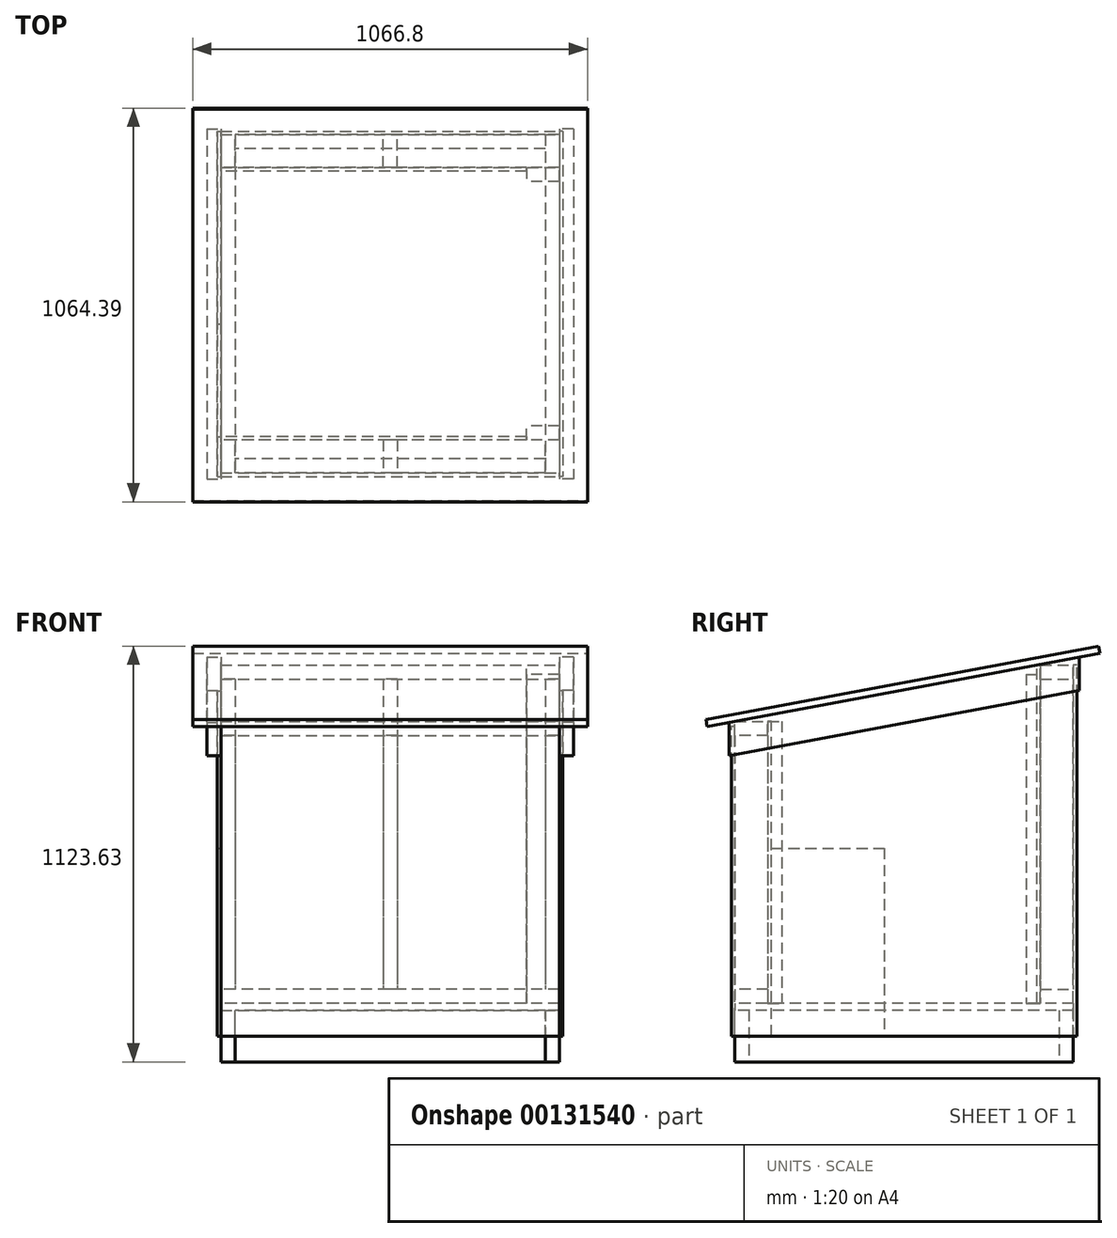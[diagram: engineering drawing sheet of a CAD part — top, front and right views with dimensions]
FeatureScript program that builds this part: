
annotation { "Feature Type Name" : "Feature", "Feature Type Description" : "" }
export const myFeature = defineFeature(function(context is Context, id is Id, definition is map)
    precondition{}
    {
        {
            var Q0;
            Q0=qCreatedBy(makeId("Front.planeOp"),FACE);
            var sketch = newSketch(context, id + "F0", { "sketchPlane" : qUnion([Q0])});
            skLineSegment(sketch, "E0.bottom", {"start": v(0, 0) * mm, "end": v(38.1, 0) * mm});
            skLineSegment(sketch, "E0.top", {"start": v(0, 139.7) * mm, "end": v(38.1, 139.7) * mm});
            skLineSegment(sketch, "E0.left", {"start": v(0, 0) * mm, "end": v(0, 139.7) * mm});
            skLineSegment(sketch, "E0.right", {"start": v(38.1, 0) * mm, "end": v(38.1, 139.7) * mm});
            skSolve(sketch);
        }
        {
            var Q0;
            Q0=qSketchRegion(id+"F0",true);
            extrude(context, id + "F1", {"entities" : qUnion([Q0]), "oppositeDirection" : true, "depth" : 914.4 * mm});
        }
        {
            var Q0;
            Q0=qCreatedBy(makeId("Front.planeOp"),FACE);
            var sketch = newSketch(context, id + "F2", { "sketchPlane" : qUnion([Q0])});
            skLineSegment(sketch, "E1.bottom", {"start": v(876.3, 0) * mm, "end": v(914.4, 0) * mm});
            skLineSegment(sketch, "E1.top", {"start": v(876.3, 139.7) * mm, "end": v(914.4, 139.7) * mm});
            skLineSegment(sketch, "E1.left", {"start": v(876.3, 0) * mm, "end": v(876.3, 139.7) * mm});
            skLineSegment(sketch, "E1.right", {"start": v(914.4, 0) * mm, "end": v(914.4, 139.7) * mm});
            skSolve(sketch);
        }
        {
            var Q0;
            Q0=makeQuery(id+"F2.imprint","IMPRINT",FACE,{"disambiguationData":[TD([[makeQuery(id+"F2.imprint","IMPRINT",EDGE,{"derivedFrom":sQuery(id+"F2.wireOp",EDGE,"E1.bottom")}),1.0]])]});
            var Q1;
            Q1=makeQuery(id+"F1.opExtrude","CAP_FACE",FACE,{"disambiguationData":[OSD([sQuery(id+"F0.wireOp",EDGE,"E0.bottom"),sQuery(id+"F0.wireOp",EDGE,"E0.top"),sQuery(id+"F0.wireOp",EDGE,"E0.left"),sQuery(id+"F0.wireOp",EDGE,"E0.right")])],"isStart":false});
            extrude(context, id + "F3", {"entities" : qUnion([Q0]), "endBound" : BoundingType.UP_TO_SURFACE, "oppositeDirection" : true, "endBoundEntityFace" : qUnion([Q1]), "depth" : 914.4 * mm});
        }
        {
            var Q0;
            Q0=makeQuery(id+"F1.opExtrude","SWEPT_FACE",FACE,{"disambiguationData":[OSD([sQuery(id+"F0.wireOp",EDGE,"E0.right")])]});
            var sketch = newSketch(context, id + "F4", { "sketchPlane" : qUnion([Q0])});
            skLineSegment(sketch, "E2.bottom", {"start": v(914.4, 139.7) * mm, "end": v(876.3, 139.7) * mm});
            skLineSegment(sketch, "E2.top", {"start": v(914.4, 0) * mm, "end": v(876.3, 0) * mm});
            skLineSegment(sketch, "E2.left", {"start": v(914.4, 139.7) * mm, "end": v(914.4, 0) * mm});
            skLineSegment(sketch, "E2.right", {"start": v(876.3, 139.7) * mm, "end": v(876.3, 0) * mm});
            skSolve(sketch);
        }
        {
            var Q0;
            Q0=qSketchRegion(id+"F4",true);
            var Q1;
            Q1=makeQuery(id+"F3.opExtrude","SWEPT_BODY",BODY,{"disambiguationData":[OSD([sQuery(id+"F2.wireOp",EDGE,"E1.bottom"),sQuery(id+"F2.wireOp",EDGE,"E1.top"),sQuery(id+"F2.wireOp",EDGE,"E1.left"),sQuery(id+"F2.wireOp",EDGE,"E1.right")])]});
            extrude(context, id + "F5", {"entities" : qUnion([Q0]), "endBound" : BoundingType.UP_TO_BODY, "endBoundEntityBody" : qUnion([Q1]), "depth" : 25.4 * mm});
        }
        {
            var Q0;
            Q0=makeQuery(id+"F1.opExtrude","SWEPT_FACE",FACE,{"disambiguationData":[OSD([sQuery(id+"F0.wireOp",EDGE,"E0.right")])]});
            var sketch = newSketch(context, id + "F6", { "sketchPlane" : qUnion([Q0])});
            skLineSegment(sketch, "E3.bottom", {"start": v(0, 139.7) * mm, "end": v(38.1, 139.7) * mm});
            skLineSegment(sketch, "E3.top", {"start": v(0, 0) * mm, "end": v(38.1, 0) * mm});
            skLineSegment(sketch, "E3.left", {"start": v(0, 139.7) * mm, "end": v(0, 0) * mm});
            skLineSegment(sketch, "E3.right", {"start": v(38.1, 139.7) * mm, "end": v(38.1, 0) * mm});
            skSolve(sketch);
        }
        {
            var Q0;
            Q0=qSketchRegion(id+"F6",true);
            var Q1;
            Q1=makeQuery(id+"F3.opExtrude","SWEPT_BODY",BODY,{"disambiguationData":[OSD([sQuery(id+"F2.wireOp",EDGE,"E1.bottom"),sQuery(id+"F2.wireOp",EDGE,"E1.top"),sQuery(id+"F2.wireOp",EDGE,"E1.left"),sQuery(id+"F2.wireOp",EDGE,"E1.right")])]});
            extrude(context, id + "F7", {"entities" : qUnion([Q0]), "endBound" : BoundingType.UP_TO_BODY, "endBoundEntityBody" : qUnion([Q1]), "depth" : 25.4 * mm});
        }
        {
            var Q0;
            Q0=makeQuery(id+"F1.opExtrude","SWEPT_FACE",FACE,{"disambiguationData":[OSD([sQuery(id+"F0.wireOp",EDGE,"E0.top")])]});
            var sketch = newSketch(context, id + "F8", { "sketchPlane" : qUnion([Q0])});
            skLineSegment(sketch, "E4.bottom", {"start": v(0, 0) * mm, "end": v(914.4, 0) * mm});
            skLineSegment(sketch, "E4.top", {"start": v(0, 914.4) * mm, "end": v(914.4, 914.4) * mm});
            skLineSegment(sketch, "E4.left", {"start": v(0, 0) * mm, "end": v(0, 914.4) * mm});
            skLineSegment(sketch, "E4.right", {"start": v(914.4, 0) * mm, "end": v(914.4, 914.4) * mm});
            skSolve(sketch);
        }
        {
            var Q0;
            Q0=qSketchRegion(id+"F8",true);
            extrude(context, id + "F9", {"entities" : qUnion([Q0]), "depth" : 19.05 * mm});
        }
        {
            var Q0;
            Q0=makeQuery(id+"F1.opExtrude","SWEPT_FACE",FACE,{"disambiguationData":[OSD([sQuery(id+"F0.wireOp",EDGE,"E0.left")])]});
            var sketch = newSketch(context, id + "F10", { "sketchPlane" : qUnion([Q0])});
            skLineSegment(sketch, "E5.bottom", {"start": v(0, 158.75) * mm, "end": v(-88.9, 158.75) * mm});
            skLineSegment(sketch, "E5.top", {"start": v(0, 196.85) * mm, "end": v(-88.9, 196.85) * mm});
            skLineSegment(sketch, "E5.left", {"start": v(0, 158.75) * mm, "end": v(0, 196.85) * mm});
            skLineSegment(sketch, "E5.right", {"start": v(-88.9, 158.75) * mm, "end": v(-88.9, 196.85) * mm});
            skSolve(sketch);
        }
        {
            var Q0;
            Q0=qSketchRegion(id+"F10",true);
            var Q1;
            Q1=makeQuery(id+"F9.opExtrude","SWEPT_FACE",FACE,{"disambiguationData":[OSD([sQuery(id+"F8.wireOp",EDGE,"E4.right")])]});
            extrude(context, id + "F11", {"entities" : qUnion([Q0]), "endBound" : BoundingType.UP_TO_SURFACE, "oppositeDirection" : true, "endBoundEntityFace" : qUnion([Q1]), "depth" : 25.4 * mm});
        }
        {
            var Q0;
            Q0=makeQuery(id+"F1.opExtrude","SWEPT_FACE",FACE,{"disambiguationData":[OSD([sQuery(id+"F0.wireOp",EDGE,"E0.left")])]});
            var sketch = newSketch(context, id + "F12", { "sketchPlane" : qUnion([Q0])});
            skLineSegment(sketch, "E6.bottom", {"start": v(-914.4, 158.75) * mm, "end": v(-825.5, 158.75) * mm});
            skLineSegment(sketch, "E6.top", {"start": v(-914.4, 196.85) * mm, "end": v(-825.5, 196.85) * mm});
            skLineSegment(sketch, "E6.left", {"start": v(-914.4, 158.75) * mm, "end": v(-914.4, 196.85) * mm});
            skLineSegment(sketch, "E6.right", {"start": v(-825.5, 158.75) * mm, "end": v(-825.5, 196.85) * mm});
            skSolve(sketch);
        }
        {
            var Q0;
            Q0=qSketchRegion(id+"F12",true);
            var Q1;
            Q1=makeQuery(id+"F3.opExtrude","SWEPT_FACE",FACE,{"disambiguationData":[OSD([sQuery(id+"F2.wireOp",EDGE,"E1.right")])]});
            extrude(context, id + "F13", {"entities" : qUnion([Q0]), "endBound" : BoundingType.UP_TO_SURFACE, "oppositeDirection" : true, "endBoundEntityFace" : qUnion([Q1]), "depth" : 25.4 * mm});
        }
        {
            var Q0;
            Q0=makeQuery(id+"F13.opExtrude","SWEPT_FACE",FACE,{"disambiguationData":[OSD([sQuery(id+"F12.wireOp",EDGE,"E6.top")])]});
            var sketch = newSketch(context, id + "F14", { "sketchPlane" : qUnion([Q0])});
            skLineSegment(sketch, "E7.bottom", {"start": v(914.4, 914.4) * mm, "end": v(876.3, 914.4) * mm});
            skLineSegment(sketch, "E7.top", {"start": v(914.4, 825.5) * mm, "end": v(876.3, 825.5) * mm});
            skLineSegment(sketch, "E7.left", {"start": v(914.4, 914.4) * mm, "end": v(914.4, 825.5) * mm});
            skLineSegment(sketch, "E7.right", {"start": v(876.3, 914.4) * mm, "end": v(876.3, 825.5) * mm});
            skSolve(sketch);
        }
        {
            var Q0;
            Q0=qSketchRegion(id+"F14",true);
            extrude(context, id + "F15", {"entities" : qUnion([Q0]), "depth" : 838.2 * mm});
        }
        {
            var Q0;
            Q0=makeQuery(id+"F13.opExtrude","SWEPT_FACE",FACE,{"disambiguationData":[OSD([sQuery(id+"F12.wireOp",EDGE,"E6.top")])]});
            var sketch = newSketch(context, id + "F16", { "sketchPlane" : qUnion([Q0])});
            skLineSegment(sketch, "E8.bottom", {"start": v(0, 825.5) * mm, "end": v(38.1, 825.5) * mm});
            skLineSegment(sketch, "E8.top", {"start": v(0, 914.4) * mm, "end": v(38.1, 914.4) * mm});
            skLineSegment(sketch, "E8.left", {"start": v(0, 825.5) * mm, "end": v(0, 914.4) * mm});
            skLineSegment(sketch, "E8.right", {"start": v(38.1, 825.5) * mm, "end": v(38.1, 914.4) * mm});
            skSolve(sketch);
        }
        {
            var Q0;
            Q0=qSketchRegion(id+"F16",true);
            var Q1;
            Q1=makeQuery(id+"F15.opExtrude","CAP_FACE",FACE,{"disambiguationData":[OSD([sQuery(id+"F14.wireOp",EDGE,"E7.bottom"),sQuery(id+"F14.wireOp",EDGE,"E7.top"),sQuery(id+"F14.wireOp",EDGE,"E7.left"),sQuery(id+"F14.wireOp",EDGE,"E7.right")])],"isStart":false});
            extrude(context, id + "F17", {"entities" : qUnion([Q0]), "endBound" : BoundingType.UP_TO_SURFACE, "endBoundEntityFace" : qUnion([Q1]), "depth" : 25.4 * mm});
        }
        {
            var Q0;
            Q0=makeQuery(id+"F13.opExtrude","SWEPT_FACE",FACE,{"disambiguationData":[OSD([sQuery(id+"F12.wireOp",EDGE,"E6.top")])]});
            var sketch = newSketch(context, id + "F18", { "sketchPlane" : qUnion([Q0])});
            skLineSegment(sketch, "E9.bottom", {"start": v(438.15, 825.5) * mm, "end": v(476.25, 825.5) * mm});
            skLineSegment(sketch, "E9.top", {"start": v(438.15, 914.4) * mm, "end": v(476.25, 914.4) * mm});
            skLineSegment(sketch, "E9.left", {"start": v(438.15, 825.5) * mm, "end": v(438.15, 914.4) * mm});
            skLineSegment(sketch, "E9.right", {"start": v(476.25, 825.5) * mm, "end": v(476.25, 914.4) * mm});
            skSolve(sketch);
        }
        {
            var Q0;
            Q0=qSketchRegion(id+"F18",true);
            var Q1;
            Q1=makeQuery(id+"F15.opExtrude","CAP_FACE",FACE,{"disambiguationData":[OSD([sQuery(id+"F14.wireOp",EDGE,"E7.bottom"),sQuery(id+"F14.wireOp",EDGE,"E7.top"),sQuery(id+"F14.wireOp",EDGE,"E7.left"),sQuery(id+"F14.wireOp",EDGE,"E7.right")])],"isStart":false});
            extrude(context, id + "F19", {"entities" : qUnion([Q0]), "endBound" : BoundingType.UP_TO_SURFACE, "endBoundEntityFace" : qUnion([Q1]), "depth" : 25.4 * mm});
        }
        {
            var Q0;
            Q0=makeQuery(id+"F15.opExtrude","SWEPT_FACE",FACE,{"disambiguationData":[OSD([sQuery(id+"F14.wireOp",EDGE,"E7.left")])]});
            var sketch = newSketch(context, id + "F20", { "sketchPlane" : qUnion([Q0])});
            skLineSegment(sketch, "E10.bottom", {"start": v(914.4, 1035.05) * mm, "end": v(825.5, 1035.05) * mm});
            skLineSegment(sketch, "E10.top", {"start": v(914.4, 1073.15) * mm, "end": v(825.5, 1073.15) * mm});
            skLineSegment(sketch, "E10.left", {"start": v(914.4, 1035.05) * mm, "end": v(914.4, 1073.15) * mm});
            skLineSegment(sketch, "E10.right", {"start": v(825.5, 1035.05) * mm, "end": v(825.5, 1073.15) * mm});
            skSolve(sketch);
        }
        {
            var Q0;
            Q0=qSketchRegion(id+"F20",true);
            var Q1;
            Q1=makeQuery(id+"F17.opExtrude","SWEPT_FACE",FACE,{"disambiguationData":[OSD([sQuery(id+"F16.wireOp",EDGE,"E8.left")])]});
            extrude(context, id + "F21", {"entities" : qUnion([Q0]), "endBound" : BoundingType.UP_TO_SURFACE, "oppositeDirection" : true, "endBoundEntityFace" : qUnion([Q1]), "depth" : 25.4 * mm});
        }
        {
            var Q0;
            Q0=makeQuery(id+"F11.opExtrude","SWEPT_FACE",FACE,{"disambiguationData":[OSD([sQuery(id+"F10.wireOp",EDGE,"E5.top")])]});
            var sketch = newSketch(context, id + "F22", { "sketchPlane" : qUnion([Q0])});
            skLineSegment(sketch, "E11.bottom", {"start": v(914.4, 0) * mm, "end": v(876.3, 0) * mm});
            skLineSegment(sketch, "E11.top", {"start": v(914.4, 88.9) * mm, "end": v(876.3, 88.9) * mm});
            skLineSegment(sketch, "E11.left", {"start": v(914.4, 0) * mm, "end": v(914.4, 88.9) * mm});
            skLineSegment(sketch, "E11.right", {"start": v(876.3, 0) * mm, "end": v(876.3, 88.9) * mm});
            skSolve(sketch);
        }
        {
            var Q0;
            Q0=qSketchRegion(id+"F22",true);
            extrude(context, id + "F23", {"entities" : qUnion([Q0]), "depth" : 685.8 * mm});
        }
        {
            var Q0;
            Q0=makeQuery(id+"F11.opExtrude","SWEPT_FACE",FACE,{"disambiguationData":[OSD([sQuery(id+"F10.wireOp",EDGE,"E5.top")])]});
            var sketch = newSketch(context, id + "F24", { "sketchPlane" : qUnion([Q0])});
            skLineSegment(sketch, "E12.bottom", {"start": v(0, 0) * mm, "end": v(38.1, 0) * mm});
            skLineSegment(sketch, "E12.top", {"start": v(0, 88.9) * mm, "end": v(38.1, 88.9) * mm});
            skLineSegment(sketch, "E12.left", {"start": v(0, 0) * mm, "end": v(0, 88.9) * mm});
            skLineSegment(sketch, "E12.right", {"start": v(38.1, 0) * mm, "end": v(38.1, 88.9) * mm});
            skSolve(sketch);
        }
        {
            var Q0;
            Q0=qSketchRegion(id+"F24",true);
            var Q1;
            Q1=makeQuery(id+"F23.opExtrude","CAP_FACE",FACE,{"disambiguationData":[OSD([sQuery(id+"F22.wireOp",EDGE,"E11.bottom"),sQuery(id+"F22.wireOp",EDGE,"E11.top"),sQuery(id+"F22.wireOp",EDGE,"E11.left"),sQuery(id+"F22.wireOp",EDGE,"E11.right")])],"isStart":false});
            extrude(context, id + "F25", {"entities" : qUnion([Q0]), "endBound" : BoundingType.UP_TO_SURFACE, "endBoundEntityFace" : qUnion([Q1]), "depth" : 25.4 * mm});
        }
        {
            var Q0;
            Q0=makeQuery(id+"F11.opExtrude","SWEPT_FACE",FACE,{"disambiguationData":[OSD([sQuery(id+"F10.wireOp",EDGE,"E5.top")])]});
            var sketch = newSketch(context, id + "F26", { "sketchPlane" : qUnion([Q0])});
            skLineSegment(sketch, "E13.bottom", {"start": v(438.15, 88.9) * mm, "end": v(476.25, 88.9) * mm});
            skLineSegment(sketch, "E13.top", {"start": v(438.15, 0) * mm, "end": v(476.25, 0) * mm});
            skLineSegment(sketch, "E13.left", {"start": v(438.15, 88.9) * mm, "end": v(438.15, 0) * mm});
            skLineSegment(sketch, "E13.right", {"start": v(476.25, 88.9) * mm, "end": v(476.25, 0) * mm});
            skSolve(sketch);
        }
        {
            var Q0;
            Q0=qSketchRegion(id+"F26",true);
            var Q1;
            Q1=makeQuery(id+"F23.opExtrude","CAP_FACE",FACE,{"disambiguationData":[OSD([sQuery(id+"F22.wireOp",EDGE,"E11.bottom"),sQuery(id+"F22.wireOp",EDGE,"E11.top"),sQuery(id+"F22.wireOp",EDGE,"E11.left"),sQuery(id+"F22.wireOp",EDGE,"E11.right")])],"isStart":false});
            extrude(context, id + "F27", {"entities" : qUnion([Q0]), "endBound" : BoundingType.UP_TO_SURFACE, "endBoundEntityFace" : qUnion([Q1]), "depth" : 25.4 * mm});
        }
        {
            var Q0;
            Q0=makeQuery(id+"F23.opExtrude","SWEPT_FACE",FACE,{"disambiguationData":[OSD([sQuery(id+"F22.wireOp",EDGE,"E11.left")])]});
            var sketch = newSketch(context, id + "F28", { "sketchPlane" : qUnion([Q0])});
            skLineSegment(sketch, "E14.bottom", {"start": v(0, 882.65) * mm, "end": v(88.9, 882.65) * mm});
            skLineSegment(sketch, "E14.top", {"start": v(0, 920.75) * mm, "end": v(88.9, 920.75) * mm});
            skLineSegment(sketch, "E14.left", {"start": v(0, 882.65) * mm, "end": v(0, 920.75) * mm});
            skLineSegment(sketch, "E14.right", {"start": v(88.9, 882.65) * mm, "end": v(88.9, 920.75) * mm});
            skSolve(sketch);
        }
        {
            var Q0;
            Q0=qSketchRegion(id+"F28",true);
            var Q1;
            Q1=makeQuery(id+"F25.opExtrude","SWEPT_FACE",FACE,{"disambiguationData":[OSD([sQuery(id+"F24.wireOp",EDGE,"E12.left")])]});
            extrude(context, id + "F29", {"entities" : qUnion([Q0]), "endBound" : BoundingType.UP_TO_SURFACE, "oppositeDirection" : true, "endBoundEntityFace" : qUnion([Q1]), "depth" : 25.4 * mm});
        }
        {
            var Q0;
            Q0=makeQuery(id+"F13.opExtrude","SWEPT_FACE",FACE,{"disambiguationData":[OSD([sQuery(id+"F12.wireOp",EDGE,"E6.right")])]});
            var sketch = newSketch(context, id + "F30", { "sketchPlane" : qUnion([Q0])});
            skLineSegment(sketch, "E15.bottom", {"start": v(0, 158.75) * mm, "end": v(825.5, 158.75) * mm});
            skLineSegment(sketch, "E15.top", {"start": v(0, 1073.15) * mm, "end": v(825.5, 1073.15) * mm});
            skLineSegment(sketch, "E15.left", {"start": v(0, 158.75) * mm, "end": v(0, 1073.15) * mm});
            skLineSegment(sketch, "E15.right", {"start": v(825.5, 158.75) * mm, "end": v(825.5, 1073.15) * mm});
            skSolve(sketch);
        }
        {
            var Q0;
            Q0=qSketchRegion(id+"F30",true);
            extrude(context, id + "F31", {"entities" : qUnion([Q0]), "depth" : 9.52 * mm});
        }
        {
            var Q0;
            Q0=makeQuery(id+"F11.opExtrude","SWEPT_FACE",FACE,{"disambiguationData":[OSD([sQuery(id+"F10.wireOp",EDGE,"E5.right")])]});
            var sketch = newSketch(context, id + "F32", { "sketchPlane" : qUnion([Q0])});
            skLineSegment(sketch, "E16.bottom", {"start": v(0, 158.75) * mm, "end": v(-825.5, 158.75) * mm});
            skLineSegment(sketch, "E16.top", {"start": v(0, 920.75) * mm, "end": v(-825.5, 920.75) * mm});
            skLineSegment(sketch, "E16.left", {"start": v(0, 158.75) * mm, "end": v(0, 920.75) * mm});
            skLineSegment(sketch, "E16.right", {"start": v(-825.5, 158.75) * mm, "end": v(-825.5, 920.75) * mm});
            skSolve(sketch);
        }
        {
            var Q0;
            Q0=qSketchRegion(id+"F32",true);
            extrude(context, id + "F33", {"entities" : qUnion([Q0]), "depth" : 9.52 * mm});
        }
        {
            var Q0;
            Q0=makeQuery(id+"F31.opExtrude","CAP_VERTEX",VERTEX,{"disambiguationData":[OSD([sQuery(id+"F30.wireOp",EDGE,"E15.top"),sQuery(id+"F30.wireOp",EDGE,"E15.left")])],"isStart":false});
            var Q1;
            Q1=makeQuery(id+"F31.opExtrude","CAP_VERTEX",VERTEX,{"disambiguationData":[OSD([sQuery(id+"F30.wireOp",EDGE,"E15.top"),sQuery(id+"F30.wireOp",EDGE,"E15.right")])],"isStart":false});
            var Q2;
            Q2=makeQuery(id+"F29.opExtrude","CAP_VERTEX",VERTEX,{"disambiguationData":[OSD([sQuery(id+"F28.wireOp",EDGE,"E14.top"),sQuery(id+"F28.wireOp",EDGE,"E14.left")])],"isStart":true});
            cPlane(context, id + "F34", {"entities" : qUnion([Q0, Q1, Q2]), "cplaneType" : CPlaneType.THREE_POINT, "offset" : 152.4 * mm, "width" : 152.4 * mm, "height" : 152.4 * mm});
        }
        {
            var Q0;
            Q0=qCreatedBy(id+"F34.planeOp",FACE);
            var sketch = newSketch(context, id + "F35", { "sketchPlane" : qUnion([Q0])});
            skLineSegment(sketch, "E17.bottom", {"start": v(-76.2, 92.85) * mm, "end": v(990.6, 92.85) * mm});
            skLineSegment(sketch, "E17.top", {"start": v(-76.2, 1172.08) * mm, "end": v(990.6, 1172.08) * mm});
            skLineSegment(sketch, "E17.left", {"start": v(-76.2, 92.85) * mm, "end": v(-76.2, 1172.08) * mm});
            skLineSegment(sketch, "E17.right", {"start": v(990.6, 92.85) * mm, "end": v(990.6, 1172.08) * mm});
            skSolve(sketch);
        }
        {
            var Q0;
            Q0=qSketchRegion(id+"F35",true);
            extrude(context, id + "F36", {"entities" : qUnion([Q0]), "depth" : 19.05 * mm});
        }
        {
            var Q0;
            Q0=makeQuery(id+"F1.opExtrude","CAP_FACE",FACE,{"disambiguationData":[OSD([sQuery(id+"F0.wireOp",EDGE,"E0.bottom"),sQuery(id+"F0.wireOp",EDGE,"E0.top"),sQuery(id+"F0.wireOp",EDGE,"E0.left"),sQuery(id+"F0.wireOp",EDGE,"E0.right")])],"isStart":false});
            var sketch = newSketch(context, id + "F37", { "sketchPlane" : qUnion([Q0])});
            skLineSegment(sketch, "E18.bottom", {"start": v(0, 69.85) * mm, "end": v(-914.4, 69.85) * mm});
            skLineSegment(sketch, "E18.top", {"start": v(0, 1073.15) * mm, "end": v(-914.4, 1073.15) * mm});
            skLineSegment(sketch, "E18.left", {"start": v(0, 69.85) * mm, "end": v(0, 1073.15) * mm});
            skLineSegment(sketch, "E18.right", {"start": v(-914.4, 69.85) * mm, "end": v(-914.4, 1073.15) * mm});
            skSolve(sketch);
        }
        {
            var Q0;
            Q0=qSketchRegion(id+"F37",true);
            extrude(context, id + "F38", {"entities" : qUnion([Q0]), "depth" : 9.52 * mm});
        }
        {
            var Q0;
            Q0=makeQuery(id+"F1.opExtrude","CAP_FACE",FACE,{"disambiguationData":[OSD([sQuery(id+"F0.wireOp",EDGE,"E0.bottom"),sQuery(id+"F0.wireOp",EDGE,"E0.top"),sQuery(id+"F0.wireOp",EDGE,"E0.left"),sQuery(id+"F0.wireOp",EDGE,"E0.right")])],"isStart":true});
            var sketch = newSketch(context, id + "F39", { "sketchPlane" : qUnion([Q0])});
            skLineSegment(sketch, "E19.bottom", {"start": v(0, 69.85) * mm, "end": v(914.4, 69.85) * mm});
            skLineSegment(sketch, "E19.top", {"start": v(0, 908.05) * mm, "end": v(914.4, 908.05) * mm});
            skLineSegment(sketch, "E19.left", {"start": v(0, 69.85) * mm, "end": v(0, 908.05) * mm});
            skLineSegment(sketch, "E19.right", {"start": v(914.4, 69.85) * mm, "end": v(914.4, 908.05) * mm});
            skSolve(sketch);
        }
        {
            var Q0;
            Q0=qSketchRegion(id+"F39",true);
            extrude(context, id + "F40", {"entities" : qUnion([Q0]), "depth" : 9.52 * mm});
        }
        {
            var Q0;
            Q0=makeQuery(id+"F21.opExtrude","CAP_FACE",FACE,{"disambiguationData":[OSD([sQuery(id+"F20.wireOp",EDGE,"E10.bottom"),sQuery(id+"F20.wireOp",EDGE,"E10.top"),sQuery(id+"F20.wireOp",EDGE,"E10.left"),sQuery(id+"F20.wireOp",EDGE,"E10.right")])],"isStart":false});
            var sketch = newSketch(context, id + "F41", { "sketchPlane" : qUnion([Q0])});
            skLineSegment(sketch, "E20", {"start": v(-930.28, 1094.5) * mm, "end": v(15.87, 917.79) * mm});
            skLineSegment(sketch, "E21", {"start": v(15.87, 917.79) * mm, "end": v(15.87, 827.35) * mm});
            skLineSegment(sketch, "E22", {"start": v(15.87, 827.35) * mm, "end": v(-930.27, 1004.06) * mm});
            skLineSegment(sketch, "E23", {"start": v(-930.28, 1004.06) * mm, "end": v(-930.28, 1094.5) * mm});
            skSolve(sketch);
        }
        {
            var Q0;
            Q0=qSketchRegion(id+"F41",true);
            extrude(context, id + "F42", {"entities" : qUnion([Q0]), "depth" : 38.1 * mm});
        }
        {
            var Q0;
            Q0=makeQuery(id+"F21.opExtrude","CAP_FACE",FACE,{"disambiguationData":[OSD([sQuery(id+"F20.wireOp",EDGE,"E10.bottom"),sQuery(id+"F20.wireOp",EDGE,"E10.top"),sQuery(id+"F20.wireOp",EDGE,"E10.left"),sQuery(id+"F20.wireOp",EDGE,"E10.right")])],"isStart":true});
            var sketch = newSketch(context, id + "F43", { "sketchPlane" : qUnion([Q0])});
            skLineSegment(sketch, "E24", {"start": v(-15.88, 917.79) * mm, "end": v(-15.87, 827.35) * mm});
            skLineSegment(sketch, "E25", {"start": v(-15.88, 827.35) * mm, "end": v(930.28, 1004.06) * mm});
            skLineSegment(sketch, "E26", {"start": v(930.28, 1004.06) * mm, "end": v(930.28, 1094.5) * mm});
            skLineSegment(sketch, "E27", {"start": v(930.28, 1094.5) * mm, "end": v(-15.88, 917.79) * mm});
            skSolve(sketch);
        }
        {
            var Q0;
            Q0=qSketchRegion(id+"F43",true);
            extrude(context, id + "F44", {"entities" : qUnion([Q0]), "depth" : 38.1 * mm});
        }
        {
            var Q0;
            Q0=makeQuery(id+"F9.opExtrude","CAP_FACE",FACE,{"disambiguationData":[OSD([sQuery(id+"F8.wireOp",EDGE,"E4.bottom"),sQuery(id+"F8.wireOp",EDGE,"E4.top"),sQuery(id+"F8.wireOp",EDGE,"E4.left"),sQuery(id+"F8.wireOp",EDGE,"E4.right")])],"isStart":false});
            var sketch = newSketch(context, id + "F45", { "sketchPlane" : qUnion([Q0])});
            skLineSegment(sketch, "E28.bottom", {"start": v(914.4, 825.5) * mm, "end": v(825.5, 825.5) * mm});
            skLineSegment(sketch, "E28.top", {"start": v(914.4, 787.4) * mm, "end": v(825.5, 787.4) * mm});
            skLineSegment(sketch, "E28.left", {"start": v(914.4, 825.5) * mm, "end": v(914.4, 787.4) * mm});
            skLineSegment(sketch, "E28.right", {"start": v(825.5, 825.5) * mm, "end": v(825.5, 787.4) * mm});
            skSolve(sketch);
        }
        {
            var Q0;
            Q0=qSketchRegion(id+"F45",true);
            extrude(context, id + "F46", {"entities" : qUnion([Q0]), "depth" : 889 * mm});
        }
        {
            var Q0;
            Q0=makeQuery(id+"F9.opExtrude","CAP_FACE",FACE,{"disambiguationData":[OSD([sQuery(id+"F8.wireOp",EDGE,"E4.bottom"),sQuery(id+"F8.wireOp",EDGE,"E4.top"),sQuery(id+"F8.wireOp",EDGE,"E4.left"),sQuery(id+"F8.wireOp",EDGE,"E4.right")])],"isStart":false});
            var sketch = newSketch(context, id + "F47", { "sketchPlane" : qUnion([Q0])});
            skLineSegment(sketch, "E29.bottom", {"start": v(914.4, 88.9) * mm, "end": v(825.5, 88.9) * mm});
            skLineSegment(sketch, "E29.top", {"start": v(914.4, 127) * mm, "end": v(825.5, 127) * mm});
            skLineSegment(sketch, "E29.left", {"start": v(914.4, 88.9) * mm, "end": v(914.4, 127) * mm});
            skLineSegment(sketch, "E29.right", {"start": v(825.5, 88.9) * mm, "end": v(825.5, 127) * mm});
            skSolve(sketch);
        }
        {
            var Q0;
            Q0=qSketchRegion(id+"F47",true);
            extrude(context, id + "F48", {"entities" : qUnion([Q0]), "depth" : 762 * mm});
        }
        {
            var Q0;
            Q0=makeQuery(id+"F3.opExtrude","SWEPT_FACE",FACE,{"disambiguationData":[OSD([sQuery(id+"F2.wireOp",EDGE,"E1.right")])]});
            var sketch = newSketch(context, id + "F49", { "sketchPlane" : qUnion([Q0])});
            skLineSegment(sketch, "E30.bottom", {"start": v(-9.52, 69.85) * mm, "end": v(923.93, 69.85) * mm});
            skLineSegment(sketch, "E30.left", {"start": v(-9.52, 69.85) * mm, "end": v(-9.53, 828.53) * mm});
            skLineSegment(sketch, "E30.right", {"start": v(923.93, 69.85) * mm, "end": v(923.92, 828.53) * mm});
            skLineSegment(sketch, "E31", {"start": v(-9.53, 828.53) * mm, "end": v(923.93, 1002.87) * mm});
            skLineSegment(sketch, "E32", {"start": v(923.93, 1002.87) * mm, "end": v(923.93, 828.53) * mm});
            skSolve(sketch);
        }
        {
            var Q0;
            Q0=qSketchRegion(id+"F49",true);
            extrude(context, id + "F50", {"entities" : qUnion([Q0]), "depth" : 9.52 * mm});
        }
        {
            var Q0;
            Q0=makeQuery(id+"F3.opExtrude","SWEPT_FACE",FACE,{"disambiguationData":[OSD([sQuery(id+"F2.wireOp",EDGE,"E1.right")])]});
            var sketch = newSketch(context, id + "F51", { "sketchPlane" : qUnion([Q0])});
            skLineSegment(sketch, "E33.bottom", {"start": v(-9.53, 828.53) * mm, "end": v(923.93, 828.53) * mm});
            skLineSegment(sketch, "E33.top", {"start": v(-9.53, 69.85) * mm, "end": v(923.93, 69.85) * mm});
            skLineSegment(sketch, "E33.left", {"start": v(-9.53, 828.53) * mm, "end": v(-9.52, 69.85) * mm});
            skLineSegment(sketch, "E33.right", {"start": v(923.93, 828.53) * mm, "end": v(923.93, 69.85) * mm});
            skLineSegment(sketch, "E34", {"start": v(923.93, 828.53) * mm, "end": v(923.93, 1002.87) * mm});
            skLineSegment(sketch, "E35", {"start": v(923.93, 1002.87) * mm, "end": v(-9.53, 828.53) * mm});
            skSolve(sketch);
        }
        {
            var Q0;
            Q0=qSketchRegion(id+"F51",true);
            extrude(context, id + "F52", {"entities" : qUnion([Q0]), "depth" : 9.52 * mm});
        }
        {
            var Q0;
            Q0=makeQuery(id+"F1.opExtrude","SWEPT_FACE",FACE,{"disambiguationData":[OSD([sQuery(id+"F0.wireOp",EDGE,"E0.left")])]});
            var sketch = newSketch(context, id + "F53", { "sketchPlane" : qUnion([Q0])});
            skLineSegment(sketch, "E36", {"start": v(-923.93, 69.85) * mm, "end": v(-923.93, 1002.87) * mm});
            skLineSegment(sketch, "E37", {"start": v(-923.93, 1002.87) * mm, "end": v(9.53, 828.53) * mm});
            skLineSegment(sketch, "E38", {"start": v(9.52, 828.53) * mm, "end": v(9.53, 69.85) * mm});
            skLineSegment(sketch, "E39", {"start": v(9.53, 69.85) * mm, "end": v(-98.42, 69.85) * mm});
            skLineSegment(sketch, "E40", {"start": v(-98.42, 69.85) * mm, "end": v(-98.42, 577.85) * mm});
            skLineSegment(sketch, "E41", {"start": v(-98.42, 577.85) * mm, "end": v(-403.23, 577.85) * mm});
            skLineSegment(sketch, "E42", {"start": v(-403.23, 577.85) * mm, "end": v(-403.22, 69.85) * mm});
            skLineSegment(sketch, "E43", {"start": v(-403.22, 69.85) * mm, "end": v(-923.93, 69.85) * mm});
            skSolve(sketch);
        }
        {
            var Q0;
            Q0=qSketchRegion(id+"F53",true);
            extrude(context, id + "F54", {"entities" : qUnion([Q0]), "depth" : 9.52 * mm});
        }
    });
